# Revit family: Elite_Sliding_Window_XXXX_Standard
name_source: partatom
category: Windows
revit_build: Autodesk Revit 2014 (Build: 20130308_1515(x64)
units: mm (PartAtom-declared; Revit-internal decimal feet)

## types (41) — shared parameters
Astragal Sash Gap = 1 mm  [stored 0.00328084 ft]
Centered In Wall = Yes
Custom Sash Width Side = 800 mm  [stored 2.62467 ft]
Default Sill Height = 800 mm  [stored 2.62467 ft]
Description = Sliding window, XXXX
Equal Sash Width = Yes
Frame Thickness = 70 mm
Limit Sash Height Max = 1800 mm  [stored 5.90551 ft]
Limit Sash Height Min = 300 mm  [stored 0.984252 ft]
Limit Sash Width Max = 1500 mm  [stored 4.92126 ft]
Limit Sash Width Min = 300 mm  [stored 0.984252 ft]
Limit Sash Width Side Min = 300 mm  [stored 0.984252 ft]
Limit Window Height Min = 383 mm  [stored 1.25656 ft]
Limit Window Width Min = 1167 mm
Manufacturer = Crealco
Model = Elite
Sash Frame Seal = 1 mm  [stored 0.00328084 ft]
Sash Rail Fore Aft Spacing = 5 mm  [stored 0.0164042 ft]
Sash Side Spacing = 1 mm  [stored 0.00328084 ft]
Wall Closure = By host
zero-valued in all types: Custom Frame Offset From Exterior

## per-type parameters (varying)
- Elite-2406XXXX-1000Pa: Area Middle Sash Glazing=0.23 m²; Area Side Sash Glazing=0.23 m²; Clearvue SHGC Value=0.496; Clearvue U Value=6.99; Custom Windload=1000 mm  [stored 3.28084 ft]; Custom Window Height=590 mm  [stored 1.9357 ft]; Custom Window Width=2390 mm  [stored 7.84121 ft]; Energy Advantage SHGC Value=0.447; Energy Advantage U Value=5.88; Height=590 mm  [stored 1.9357 ft]; Inside Heavy Duty Interlocker=No; Interlocker Configuration=0 mm  [stored 0 ft]; Intruderprufe LowE SHGC Value=0.418; Intruderprufe LowE U Value=5.71; Intruderprufe SHGC Value=0.472; Intruderprufe U Value=6.87; Limit Sash Width Side Max=912 mm; Limit Window Height Max=1883 mm; Limit Window Width Max=2990 mm  [stored 9.80971 ft]; Max Pane Area=0.23 m²; Outside Heavy Duty Interlocker=No; Sash Height=507 mm; Sash Width Middle=606 mm; Sash Width Sides=606 mm; URL=http://www.crealco.co.za; Width=2390 mm  [stored 7.84121 ft]; Windload Design=1000 mm  [stored 3.28084 ft]
- Elite-2706XXXX-1000Pa: Area Middle Sash Glazing=0.26 m²; Area Side Sash Glazing=0.26 m²; Clearvue SHGC Value=5.07; Clearvue U Value=6.96; Custom Windload=1000 mm  [stored 3.28084 ft]; Custom Window Height=590 mm  [stored 1.9357 ft]; Custom Window Width=2690 mm; Energy Advantage SHGC Value=0.456; Energy Advantage U Value=5.8; Height=590 mm  [stored 1.9357 ft]; Inside Heavy Duty Interlocker=No; Interlocker Configuration=0 mm  [stored 0 ft]; Intruderprufe LowE SHGC Value=0.426; Intruderprufe LowE U Value=5.64; Intruderprufe SHGC Value=0.482; Intruderprufe U Value=6.83; Limit Sash Width Side Max=1062 mm; Limit Window Height Max=1883 mm; Limit Window Width Max=2990 mm  [stored 9.80971 ft]; Max Pane Area=0.26 m²; Outside Heavy Duty Interlocker=No; Sash Height=507 mm; Sash Width Middle=681 mm; Sash Width Sides=681 mm; URL=http://www.crealco.co.za; Width=2690 mm; Windload Design=1000 mm  [stored 3.28084 ft]
- Elite-3006XXXX-1000Pa: Area Middle Sash Glazing=0.29 m²; Area Side Sash Glazing=0.29 m²; Clearvue SHGC Value=0.515; Clearvue U Value=6.93; Custom Windload=1000 mm  [stored 3.28084 ft]; Custom Window Height=590 mm  [stored 1.9357 ft]; Custom Window Width=2990 mm  [stored 9.80971 ft]; Energy Advantage SHGC Value=0.464; Energy Advantage U Value=5.74; Height=590 mm  [stored 1.9357 ft]; Inside Heavy Duty Interlocker=No; Interlocker Configuration=0 mm  [stored 0 ft]; Intruderprufe LowE SHGC Value=0.433; Intruderprufe LowE U Value=5.59; Intruderprufe SHGC Value=0.49; Intruderprufe U Value=6.8; Limit Sash Width Side Max=1212 mm; Limit Window Height Max=1883 mm; Limit Window Width Max=2990 mm  [stored 9.80971 ft]; Max Pane Area=0.29 m²; Outside Heavy Duty Interlocker=No; Sash Height=507 mm; Sash Width Middle=756 mm; Sash Width Sides=756 mm; URL=http://www.crealco.co.za; Width=2990 mm  [stored 9.80971 ft]; Windload Design=1000 mm  [stored 3.28084 ft]
- Elite-2409XXXX-1000Pa: Area Middle Sash Glazing=0.39 m²; Area Side Sash Glazing=0.39 m²; Clearvue SHGC Value=0.568; Clearvue U Value=6.82; Custom Windload=1000 mm  [stored 3.28084 ft]; Custom Window Height=890 mm  [stored 2.91995 ft]; Custom Window Width=2390 mm  [stored 7.84121 ft]; Energy Advantage SHGC Value=0.51; Energy Advantage U Value=5.5; Height=890 mm  [stored 2.91995 ft]; Inside Heavy Duty Interlocker=No; Interlocker Configuration=0 mm  [stored 0 ft]; Intruderprufe LowE SHGC Value=0.476; Intruderprufe LowE U Value=5.33; Intruderprufe SHGC Value=0.539; Intruderprufe U Value=6.69; Limit Sash Width Side Max=912 mm; Limit Window Height Max=1883 mm; Limit Window Width Max=2990 mm  [stored 9.80971 ft]; Max Pane Area=0.39 m²; Outside Heavy Duty Interlocker=No; Sash Height=807 mm  [stored 2.64764 ft]; Sash Width Middle=606 mm; Sash Width Sides=606 mm; URL=http://www.crealco.co.za; Width=2390 mm  [stored 7.84121 ft]; Windload Design=1000 mm  [stored 3.28084 ft]
- Elite-2709XXXX-1000Pa: Area Middle Sash Glazing=0.44 m²; Area Side Sash Glazing=0.44 m²; Clearvue SHGC Value=0.58; Clearvue U Value=6.77; Custom Windload=1000 mm  [stored 3.28084 ft]; Custom Window Height=890 mm  [stored 2.91995 ft]; Custom Window Width=2690 mm; Energy Advantage SHGC Value=0.521; Energy Advantage U Value=5.41; Height=890 mm  [stored 2.91995 ft]; Inside Heavy Duty Interlocker=No; Interlocker Configuration=0 mm  [stored 0 ft]; Intruderprufe LowE SHGC Value=0.486; Intruderprufe LowE U Value=5.25; Intruderprufe SHGC Value=0.551; Intruderprufe U Value=6.64; Limit Sash Width Side Max=1062 mm; Limit Window Height Max=1883 mm; Limit Window Width Max=2990 mm  [stored 9.80971 ft]; Max Pane Area=0.44 m²; Outside Heavy Duty Interlocker=No; Sash Height=807 mm  [stored 2.64764 ft]; Sash Width Middle=681 mm; Sash Width Sides=681 mm; URL=http://www.crealco.co.za; Width=2690 mm; Windload Design=1000 mm  [stored 3.28084 ft]
- Elite-3009XXXX-1000Pa: Area Middle Sash Glazing=0.5 m²; Area Side Sash Glazing=0.5 m²; Clearvue SHGC Value=0.515; Clearvue U Value=6.93; Custom Windload=1000 mm  [stored 3.28084 ft]; Custom Window Height=890 mm  [stored 2.91995 ft]; Custom Window Width=2990 mm  [stored 9.80971 ft]; Energy Advantage SHGC Value=0.464; Energy Advantage U Value=5.74; Height=890 mm  [stored 2.91995 ft]; Inside Heavy Duty Interlocker=No; Interlocker Configuration=0 mm  [stored 0 ft]; Intruderprufe LowE SHGC Value=0.433; Intruderprufe LowE U Value=5.59; Intruderprufe SHGC Value=0.49; Intruderprufe U Value=6.8; Limit Sash Width Side Max=1212 mm; Limit Window Height Max=1883 mm; Limit Window Width Max=2990 mm  [stored 9.80971 ft]; Max Pane Area=0.5 m²; Outside Heavy Duty Interlocker=No; Sash Height=807 mm  [stored 2.64764 ft]; Sash Width Middle=756 mm; Sash Width Sides=756 mm; URL=http://www.crealco.co.za; Width=2990 mm  [stored 9.80971 ft]; Windload Design=1000 mm  [stored 3.28084 ft]
- Elite-2412XXXX-1000Pa: Area Middle Sash Glazing=0.55 m²; Area Side Sash Glazing=0.55 m²; Clearvue SHGC Value=0.603; Clearvue U Value=6.73; Custom Windload=1000 mm  [stored 3.28084 ft]; Custom Window Height=1190 mm  [stored 3.9042 ft]; Custom Window Width=2390 mm  [stored 7.84121 ft]; Energy Advantage SHGC Value=0.542; Energy Advantage U Value=5.32; Height=1190 mm  [stored 3.9042 ft]; Inside Heavy Duty Interlocker=No; Interlocker Configuration=0 mm  [stored 0 ft]; Intruderprufe LowE SHGC Value=0.505; Intruderprufe LowE U Value=5.15; Intruderprufe SHGC Value=0.572; Intruderprufe U Value=6.6; Limit Sash Width Side Max=912 mm; Limit Window Height Max=1883 mm; Limit Window Width Max=2990 mm  [stored 9.80971 ft]; Max Pane Area=0.55 m²; Outside Heavy Duty Interlocker=No; Sash Height=1107 mm  [stored 3.63189 ft]; Sash Width Middle=606 mm; Sash Width Sides=606 mm; URL=www.crealco.co.za; Width=2390 mm  [stored 7.84121 ft]; Windload Design=1000 mm  [stored 3.28084 ft]
- Elite-2712XXXX-1000Pa: Area Middle Sash Glazing=0.63 m²; Area Side Sash Glazing=0.63 m²; Clearvue SHGC Value=0.616; Clearvue U Value=6.68; Custom Windload=1000 mm  [stored 3.28084 ft]; Custom Window Height=1190 mm  [stored 3.9042 ft]; Custom Window Width=2690 mm; Energy Advantage SHGC Value=0.553; Energy Advantage U Value=5.22; Height=1190 mm  [stored 3.9042 ft]; Inside Heavy Duty Interlocker=No; Interlocker Configuration=0 mm  [stored 0 ft]; Intruderprufe LowE SHGC Value=0.515; Intruderprufe LowE U Value=5.306; Intruderprufe SHGC Value=0.585; Intruderprufe U Value=6.55; Limit Sash Width Side Max=1062 mm; Limit Window Height Max=1883 mm; Limit Window Width Max=2990 mm  [stored 9.80971 ft]; Max Pane Area=0.63 m²; Outside Heavy Duty Interlocker=No; Sash Height=1107 mm  [stored 3.63189 ft]; Sash Width Middle=681 mm; Sash Width Sides=681 mm; URL=http://www.crealco.co.za; Width=2690 mm; Windload Design=1000 mm  [stored 3.28084 ft]
- Elite-3012XXXX-1000Pa: Area Middle Sash Glazing=0.7 m²; Area Side Sash Glazing=0.7 m²; Clearvue SHGC Value=0.627; Clearvue U Value=6.64; Custom Windload=1000 mm  [stored 3.28084 ft]; Custom Window Height=1190 mm  [stored 3.9042 ft]; Custom Window Width=2990 mm  [stored 9.80971 ft]; Energy Advantage SHGC Value=0.562; Energy Advantage U Value=5.144; Height=1190 mm  [stored 3.9042 ft]; Inside Heavy Duty Interlocker=No; Interlocker Configuration=0 mm  [stored 0 ft]; Intruderprufe LowE SHGC Value=0.524; Intruderprufe LowE U Value=4.99; Intruderprufe SHGC Value=0.595; Intruderprufe U Value=6.51; Limit Sash Width Side Max=1212 mm; Limit Window Height Max=1883 mm; Limit Window Width Max=2990 mm  [stored 9.80971 ft]; Max Pane Area=0.7 m²; Outside Heavy Duty Interlocker=No; Sash Height=1107 mm  [stored 3.63189 ft]; Sash Width Middle=756 mm; Sash Width Sides=756 mm; URL=http://www.crealco.co.za; Width=2990 mm  [stored 9.80971 ft]; Windload Design=1000 mm  [stored 3.28084 ft]
- Elite-2415XXXX-1000Pa: Area Middle Sash Glazing=0.72 m²; Area Side Sash Glazing=0.72 m²; Clearvue SHGC Value=0.624; Clearvue U Value=6.68; Custom Windload=1000 mm  [stored 3.28084 ft]; Custom Window Height=1490 mm  [stored 4.88845 ft]; Custom Window Width=2390 mm  [stored 7.84121 ft]; Energy Advantage SHGC Value=0.56; Energy Advantage U Value=5.21; Height=1490 mm  [stored 4.88845 ft]; Inside Heavy Duty Interlocker=Yes; Interlocker Configuration=1 mm  [stored 0.00328084 ft]; Intruderprufe LowE SHGC Value=0.522; Intruderprufe LowE U Value=5.04; Intruderprufe SHGC Value=0.592; Intruderprufe U Value=6.55; Limit Sash Width Side Max=912 mm; Limit Window Height Max=1883 mm; Limit Window Width Max=2990 mm  [stored 9.80971 ft]; Max Pane Area=0.72 m²; Outside Heavy Duty Interlocker=No; Sash Height=1407 mm  [stored 4.61614 ft]; Sash Width Middle=606 mm; Sash Width Sides=606 mm; URL=http://www.crealco.co.za; Width=2390 mm  [stored 7.84121 ft]; Windload Design=1000 mm  [stored 3.28084 ft]
- Elite-2715XXXX-1000Pa: Area Middle Sash Glazing=0.81 m²; Area Side Sash Glazing=0.81 m²; Clearvue SHGC Value=0.638; Clearvue U Value=6.692; Custom Windload=1000 mm  [stored 3.28084 ft]; Custom Window Height=1490 mm  [stored 4.88845 ft]; Custom Window Width=2690 mm; Energy Advantage SHGC Value=0.572; Energy Advantage U Value=5.11; Height=1490 mm  [stored 4.88845 ft]; Inside Heavy Duty Interlocker=Yes; Interlocker Configuration=1 mm  [stored 0.00328084 ft]; Intruderprufe LowE SHGC Value=0.533; Intruderprufe LowE U Value=4.95; Intruderprufe SHGC Value=0.605; Intruderprufe U Value=6.49; Limit Sash Width Side Max=1062 mm; Limit Window Height Max=1883 mm; Limit Window Width Max=2990 mm  [stored 9.80971 ft]; Max Pane Area=0.81 m²; Outside Heavy Duty Interlocker=No; Sash Height=1407 mm  [stored 4.61614 ft]; Sash Width Middle=681 mm; Sash Width Sides=681 mm; URL=http://www.crealco.co.za; Width=2690 mm; Windload Design=1000 mm  [stored 3.28084 ft]
- Elite-3015XXXX-1000Pa: Area Middle Sash Glazing=0.91 m²; Area Side Sash Glazing=0.91 m²; Clearvue SHGC Value=0.649; Clearvue U Value=6.58; Custom Windload=1000 mm  [stored 3.28084 ft]; Custom Window Height=1490 mm  [stored 4.88845 ft]; Custom Window Width=2990 mm  [stored 9.80971 ft]; Energy Advantage SHGC Value=0.582; Energy Advantage U Value=5.02; Height=1490 mm  [stored 4.88845 ft]; Inside Heavy Duty Interlocker=Yes; Interlocker Configuration=1 mm  [stored 0.00328084 ft]; Intruderprufe LowE SHGC Value=0.542; Intruderprufe LowE U Value=4.87; Intruderprufe SHGC Value=0.616; Intruderprufe U Value=6.45; Limit Sash Width Side Max=1212 mm; Limit Window Height Max=1883 mm; Limit Window Width Max=2990 mm  [stored 9.80971 ft]; Max Pane Area=0.91 m²; Outside Heavy Duty Interlocker=No; Sash Height=1407 mm  [stored 4.61614 ft]; Sash Width Middle=756 mm; Sash Width Sides=756 mm; URL=http://www.crealco.co.za; Width=2990 mm  [stored 9.80971 ft]; Windload Design=1000 mm  [stored 3.28084 ft]
- Elite-2418XXXX-1000Pa: Area Middle Sash Glazing=0.88 m²; Area Side Sash Glazing=0.88 m²; Clearvue SHGC Value=0.638; Clearvue U Value=6.65; Custom Windload=1000 mm  [stored 3.28084 ft]; Custom Window Height=1790 mm  [stored 5.8727 ft]; Custom Window Width=2390 mm  [stored 7.84121 ft]; Energy Advantage SHGC Value=0.573; Energy Advantage U Value=5.13; Height=1790 mm  [stored 5.8727 ft]; Inside Heavy Duty Interlocker=Yes; Interlocker Configuration=1 mm  [stored 0.00328084 ft]; Intruderprufe LowE SHGC Value=0.533; Intruderprufe LowE U Value=4.97; Intruderprufe SHGC Value=0.606; Intruderprufe U Value=6.51; Limit Sash Width Side Max=912 mm; Limit Window Height Max=1883 mm; Limit Window Width Max=2990 mm  [stored 9.80971 ft]; Max Pane Area=0.88 m²; Outside Heavy Duty Interlocker=No; Sash Height=1707 mm; Sash Width Middle=606 mm; Sash Width Sides=606 mm; URL=http://www.crealco.co.za; Width=2390 mm  [stored 7.84121 ft]; Windload Design=1000 mm  [stored 3.28084 ft]
- Elite-2718XXXX-1000Pa: Area Middle Sash Glazing=1 m²; Area Side Sash Glazing=1 m²; Clearvue SHGC Value=0.652; Clearvue U Value=6.59; Custom Windload=1000 mm  [stored 3.28084 ft]; Custom Window Height=1790 mm  [stored 5.8727 ft]; Custom Window Width=2690 mm; Energy Advantage SHGC Value=0.585; Energy Advantage U Value=5.03; Height=1790 mm  [stored 5.8727 ft]; Inside Heavy Duty Interlocker=Yes; Interlocker Configuration=2 mm  [stored 0.00656168 ft]; Intruderprufe LowE SHGC Value=0.545; Intruderprufe LowE U Value=4.87; Intruderprufe SHGC Value=0.619; Intruderprufe U Value=6.46; Limit Sash Width Side Max=1062 mm; Limit Window Height Max=1883 mm; Limit Window Width Max=2990 mm  [stored 9.80971 ft]; Max Pane Area=1 m²; Outside Heavy Duty Interlocker=Yes; Sash Height=1707 mm; Sash Width Middle=681 mm; Sash Width Sides=681 mm; URL=http://www.crealco.co.za; Width=2690 mm; Windload Design=1000 mm  [stored 3.28084 ft]
- Elite-3018XXXX-1000Pa: Area Middle Sash Glazing=1.12 m²; Area Side Sash Glazing=1.12 m²; Clearvue SHGC Value=0.664; Clearvue U Value=6.54; Custom Windload=1000 mm  [stored 3.28084 ft]; Custom Window Height=1790 mm  [stored 5.8727 ft]; Custom Window Width=2990 mm  [stored 9.80971 ft]; Energy Advantage SHGC Value=0.595; Energy Advantage U Value=4.95; Height=1790 mm  [stored 5.8727 ft]; Inside Heavy Duty Interlocker=Yes; Interlocker Configuration=2 mm  [stored 0.00656168 ft]; Intruderprufe LowE SHGC Value=0.554; Intruderprufe LowE U Value=4.8; Intruderprufe SHGC Value=0.063; Intruderprufe U Value=6.41; Limit Sash Width Side Max=1212 mm; Limit Window Height Max=1883 mm; Limit Window Width Max=2990 mm  [stored 9.80971 ft]; Max Pane Area=1.12 m²; Outside Heavy Duty Interlocker=Yes; Sash Height=1707 mm; Sash Width Middle=756 mm; Sash Width Sides=756 mm; URL=http://www.crealco.co.za; Width=2990 mm  [stored 9.80971 ft]; Windload Design=1000 mm  [stored 3.28084 ft]
- Elite-2406XXXX-1500Pa: Area Middle Sash Glazing=0.23 m²; Area Side Sash Glazing=0.23 m²; Clearvue SHGC Value=0.496; Clearvue U Value=6.99; Custom Windload=1500 mm  [stored 4.92126 ft]; Custom Window Height=590 mm  [stored 1.9357 ft]; Custom Window Width=2390 mm  [stored 7.84121 ft]; Energy Advantage SHGC Value=0.447; Energy Advantage U Value=5.88; Height=590 mm  [stored 1.9357 ft]; Inside Heavy Duty Interlocker=No; Interlocker Configuration=0 mm  [stored 0 ft]; Intruderprufe LowE SHGC Value=0.418; Intruderprufe LowE U Value=5.71; Intruderprufe SHGC Value=0.472; Intruderprufe U Value=6.87; Limit Sash Width Side Max=912 mm; Limit Window Height Max=1883 mm; Limit Window Width Max=2990 mm  [stored 9.80971 ft]; Max Pane Area=0.23 m²; Outside Heavy Duty Interlocker=No; Sash Height=507 mm; Sash Width Middle=606 mm; Sash Width Sides=606 mm; URL=http://www.crealco.co.za; Width=2390 mm  [stored 7.84121 ft]; Windload Design=1500 mm  [stored 4.92126 ft]
- Elite-2406XXXX-2000Pa: Area Middle Sash Glazing=0.23 m²; Area Side Sash Glazing=0.23 m²; Clearvue SHGC Value=0.496; Clearvue U Value=6.99; Custom Windload=2000 mm  [stored 6.56168 ft]; Custom Window Height=590 mm  [stored 1.9357 ft]; Custom Window Width=2390 mm  [stored 7.84121 ft]; Energy Advantage SHGC Value=0.447; Energy Advantage U Value=5.88; Height=590 mm  [stored 1.9357 ft]; Inside Heavy Duty Interlocker=No; Interlocker Configuration=0 mm  [stored 0 ft]; Intruderprufe LowE SHGC Value=0.418; Intruderprufe LowE U Value=5.71; Intruderprufe SHGC Value=0.472; Intruderprufe U Value=6.87; Limit Sash Width Side Max=912 mm; Limit Window Height Max=1490 mm  [stored 4.88845 ft]; Limit Window Width Max=2990 mm  [stored 9.80971 ft]; Max Pane Area=0.23 m²; Outside Heavy Duty Interlocker=No; Sash Height=507 mm; Sash Width Middle=606 mm; Sash Width Sides=606 mm; URL=http://www.crealco.co.za; Width=2390 mm  [stored 7.84121 ft]; Windload Design=2000 mm  [stored 6.56168 ft]
- Elite-2409XXXX-1500Pa: Area Middle Sash Glazing=0.39 m²; Area Side Sash Glazing=0.39 m²; Clearvue SHGC Value=0.568; Clearvue U Value=6.82; Custom Windload=1500 mm  [stored 4.92126 ft]; Custom Window Height=890 mm  [stored 2.91995 ft]; Custom Window Width=2390 mm  [stored 7.84121 ft]; Energy Advantage SHGC Value=0.51; Energy Advantage U Value=5.5; Height=890 mm  [stored 2.91995 ft]; Inside Heavy Duty Interlocker=No; Interlocker Configuration=0 mm  [stored 0 ft]; Intruderprufe LowE SHGC Value=0.476; Intruderprufe LowE U Value=5.33; Intruderprufe SHGC Value=0.539; Intruderprufe U Value=6.69; Limit Sash Width Side Max=912 mm; Limit Window Height Max=1883 mm; Limit Window Width Max=2990 mm  [stored 9.80971 ft]; Max Pane Area=0.39 m²; Outside Heavy Duty Interlocker=No; Sash Height=807 mm  [stored 2.64764 ft]; Sash Width Middle=606 mm; Sash Width Sides=606 mm; URL=http://www.crealco.co.za; Width=2390 mm  [stored 7.84121 ft]; Windload Design=1500 mm  [stored 4.92126 ft]
- Elite-2409XXXX-2000Pa: Area Middle Sash Glazing=0.39 m²; Area Side Sash Glazing=0.39 m²; Clearvue SHGC Value=0.568; Clearvue U Value=6.82; Custom Windload=2000 mm  [stored 6.56168 ft]; Custom Window Height=890 mm  [stored 2.91995 ft]; Custom Window Width=2390 mm  [stored 7.84121 ft]; Energy Advantage SHGC Value=0.51; Energy Advantage U Value=5.5; Height=890 mm  [stored 2.91995 ft]; Inside Heavy Duty Interlocker=No; Interlocker Configuration=0 mm  [stored 0 ft]; Intruderprufe LowE SHGC Value=0.476; Intruderprufe LowE U Value=5.33; Intruderprufe SHGC Value=0.539; Intruderprufe U Value=6.69; Limit Sash Width Side Max=912 mm; Limit Window Height Max=1490 mm  [stored 4.88845 ft]; Limit Window Width Max=2990 mm  [stored 9.80971 ft]; Max Pane Area=0.39 m²; Outside Heavy Duty Interlocker=No; Sash Height=807 mm  [stored 2.64764 ft]; Sash Width Middle=606 mm; Sash Width Sides=606 mm; URL=http://www.crealco.co.za; Width=2390 mm  [stored 7.84121 ft]; Windload Design=2000 mm  [stored 6.56168 ft]
- Elite-2412XXXX-1500Pa: Area Middle Sash Glazing=0.55 m²; Area Side Sash Glazing=0.55 m²; Clearvue SHGC Value=0.603; Clearvue U Value=6.73; Custom Windload=1500 mm  [stored 4.92126 ft]; Custom Window Height=1190 mm  [stored 3.9042 ft]; Custom Window Width=2390 mm  [stored 7.84121 ft]; Energy Advantage SHGC Value=0.542; Energy Advantage U Value=5.32; Height=1190 mm  [stored 3.9042 ft]; Inside Heavy Duty Interlocker=No; Interlocker Configuration=0 mm  [stored 0 ft]; Intruderprufe LowE SHGC Value=0.505; Intruderprufe LowE U Value=5.15; Intruderprufe SHGC Value=0.572; Intruderprufe U Value=6.6; Limit Sash Width Side Max=912 mm; Limit Window Height Max=1883 mm; Limit Window Width Max=2990 mm  [stored 9.80971 ft]; Max Pane Area=0.55 m²; Outside Heavy Duty Interlocker=No; Sash Height=1107 mm  [stored 3.63189 ft]; Sash Width Middle=606 mm; Sash Width Sides=606 mm; URL=http://www.crealco.co.za; Width=2390 mm  [stored 7.84121 ft]; Windload Design=1500 mm  [stored 4.92126 ft]
- Elite-2412XXXX-2000Pa: Area Middle Sash Glazing=0.55 m²; Area Side Sash Glazing=0.55 m²; Clearvue SHGC Value=0.603; Clearvue U Value=6.73; Custom Windload=2000 mm  [stored 6.56168 ft]; Custom Window Height=1190 mm  [stored 3.9042 ft]; Custom Window Width=2390 mm  [stored 7.84121 ft]; Energy Advantage SHGC Value=0.542; Energy Advantage U Value=5.32; Height=1190 mm  [stored 3.9042 ft]; Inside Heavy Duty Interlocker=Yes; Interlocker Configuration=1 mm  [stored 0.00328084 ft]; Intruderprufe LowE SHGC Value=0.505; Intruderprufe LowE U Value=5.15; Intruderprufe SHGC Value=0.572; Intruderprufe U Value=6.6; Limit Sash Width Side Max=912 mm; Limit Window Height Max=1490 mm  [stored 4.88845 ft]; Limit Window Width Max=2990 mm  [stored 9.80971 ft]; Max Pane Area=0.55 m²; Outside Heavy Duty Interlocker=No; Sash Height=1107 mm  [stored 3.63189 ft]; Sash Width Middle=606 mm; Sash Width Sides=606 mm; URL=http://www.crealco.co.za; Width=2390 mm  [stored 7.84121 ft]; Windload Design=2000 mm  [stored 6.56168 ft]
- Elite-2415XXXX-1500Pa: Area Middle Sash Glazing=0.72 m²; Area Side Sash Glazing=0.72 m²; Clearvue SHGC Value=0.624; Clearvue U Value=6.68; Custom Windload=1500 mm  [stored 4.92126 ft]; Custom Window Height=1490 mm  [stored 4.88845 ft]; Custom Window Width=2390 mm  [stored 7.84121 ft]; Energy Advantage SHGC Value=0.56; Energy Advantage U Value=5.21; Height=1490 mm  [stored 4.88845 ft]; Inside Heavy Duty Interlocker=Yes; Interlocker Configuration=1 mm  [stored 0.00328084 ft]; Intruderprufe LowE SHGC Value=0.522; Intruderprufe LowE U Value=5.04; Intruderprufe SHGC Value=0.592; Intruderprufe U Value=6.55; Limit Sash Width Side Max=912 mm; Limit Window Height Max=1883 mm; Limit Window Width Max=2990 mm  [stored 9.80971 ft]; Max Pane Area=0.72 m²; Outside Heavy Duty Interlocker=No; Sash Height=1407 mm  [stored 4.61614 ft]; Sash Width Middle=606 mm; Sash Width Sides=606 mm; URL=http://www.crealco.co.za; Width=2390 mm  [stored 7.84121 ft]; Windload Design=1500 mm  [stored 4.92126 ft]
- Elite-2415XXXX-2000Pa: Area Middle Sash Glazing=0.72 m²; Area Side Sash Glazing=0.72 m²; Clearvue SHGC Value=0.624; Clearvue U Value=6.68; Custom Windload=2000 mm  [stored 6.56168 ft]; Custom Window Height=1490 mm  [stored 4.88845 ft]; Custom Window Width=2390 mm  [stored 7.84121 ft]; Energy Advantage SHGC Value=0.56; Energy Advantage U Value=5.21; Height=1490 mm  [stored 4.88845 ft]; Inside Heavy Duty Interlocker=Yes; Interlocker Configuration=1 mm  [stored 0.00328084 ft]; Intruderprufe LowE SHGC Value=0.522; Intruderprufe LowE U Value=5.04; Intruderprufe SHGC Value=0.592; Intruderprufe U Value=6.55; Limit Sash Width Side Max=912 mm; Limit Window Height Max=1490 mm  [stored 4.88845 ft]; Limit Window Width Max=2990 mm  [stored 9.80971 ft]; Max Pane Area=0.72 m²; Outside Heavy Duty Interlocker=No; Sash Height=1407 mm  [stored 4.61614 ft]; Sash Width Middle=606 mm; Sash Width Sides=606 mm; URL=http://www.crealco.co.za; Width=2390 mm  [stored 7.84121 ft]; Windload Design=2000 mm  [stored 6.56168 ft]
- Elite-2418XXXX-1500Pa: Area Middle Sash Glazing=0.88 m²; Area Side Sash Glazing=0.88 m²; Clearvue SHGC Value=0.638; Clearvue U Value=6.65; Custom Windload=1500 mm  [stored 4.92126 ft]; Custom Window Height=1790 mm  [stored 5.8727 ft]; Custom Window Width=2390 mm  [stored 7.84121 ft]; Energy Advantage SHGC Value=0.573; Energy Advantage U Value=5.13; Height=1790 mm  [stored 5.8727 ft]; Inside Heavy Duty Interlocker=Yes; Interlocker Configuration=2 mm  [stored 0.00656168 ft]; Intruderprufe LowE SHGC Value=0.533; Intruderprufe LowE U Value=4.97; Intruderprufe SHGC Value=0.606; Intruderprufe U Value=6.51; Limit Sash Width Side Max=912 mm; Limit Window Height Max=1883 mm; Limit Window Width Max=2690 mm; Max Pane Area=0.88 m²; Outside Heavy Duty Interlocker=Yes; Sash Height=1707 mm; Sash Width Middle=606 mm; Sash Width Sides=606 mm; URL=http://www.crealco.co.za; Width=2390 mm  [stored 7.84121 ft]; Windload Design=1500 mm  [stored 4.92126 ft]
- Elite-2706XXXX-1500Pa: Area Middle Sash Glazing=0.26 m²; Area Side Sash Glazing=0.26 m²; Clearvue SHGC Value=5.07; Clearvue U Value=6.96; Custom Windload=1500 mm  [stored 4.92126 ft]; Custom Window Height=590 mm  [stored 1.9357 ft]; Custom Window Width=2690 mm; Energy Advantage SHGC Value=0.456; Energy Advantage U Value=5.8; Height=590 mm  [stored 1.9357 ft]; Inside Heavy Duty Interlocker=No; Interlocker Configuration=0 mm  [stored 0 ft]; Intruderprufe LowE SHGC Value=0.426; Intruderprufe LowE U Value=5.64; Intruderprufe SHGC Value=0.482; Intruderprufe U Value=6.83; Limit Sash Width Side Max=1062 mm; Limit Window Height Max=1883 mm; Limit Window Width Max=2990 mm  [stored 9.80971 ft]; Max Pane Area=0.26 m²; Outside Heavy Duty Interlocker=No; Sash Height=507 mm; Sash Width Middle=681 mm; Sash Width Sides=681 mm; URL=http://www.crealco.co.za; Width=2690 mm; Windload Design=1500 mm  [stored 4.92126 ft]
- Elite-2706XXXX-2000Pa: Area Middle Sash Glazing=0.26 m²; Area Side Sash Glazing=0.26 m²; Clearvue SHGC Value=5.07; Clearvue U Value=6.96; Custom Windload=2000 mm  [stored 6.56168 ft]; Custom Window Height=590 mm  [stored 1.9357 ft]; Custom Window Width=2690 mm; Energy Advantage SHGC Value=0.456; Energy Advantage U Value=5.8; Height=590 mm  [stored 1.9357 ft]; Inside Heavy Duty Interlocker=No; Interlocker Configuration=0 mm  [stored 0 ft]; Intruderprufe LowE SHGC Value=0.426; Intruderprufe LowE U Value=5.64; Intruderprufe SHGC Value=0.482; Intruderprufe U Value=6.83; Limit Sash Width Side Max=1062 mm; Limit Window Height Max=1490 mm  [stored 4.88845 ft]; Limit Window Width Max=2990 mm  [stored 9.80971 ft]; Max Pane Area=0.26 m²; Outside Heavy Duty Interlocker=No; Sash Height=507 mm; Sash Width Middle=681 mm; Sash Width Sides=681 mm; URL=http://www.crealco.co.za; Width=2690 mm; Windload Design=2000 mm  [stored 6.56168 ft]
- Elite-2709XXXX-1500Pa: Area Middle Sash Glazing=0.44 m²; Area Side Sash Glazing=0.44 m²; Clearvue SHGC Value=0.58; Clearvue U Value=6.77; Custom Windload=1500 mm  [stored 4.92126 ft]; Custom Window Height=890 mm  [stored 2.91995 ft]; Custom Window Width=2690 mm; Energy Advantage SHGC Value=0.521; Energy Advantage U Value=5.41; Height=890 mm  [stored 2.91995 ft]; Inside Heavy Duty Interlocker=No; Interlocker Configuration=0 mm  [stored 0 ft]; Intruderprufe LowE SHGC Value=0.486; Intruderprufe LowE U Value=5.25; Intruderprufe SHGC Value=0.551; Intruderprufe U Value=6.64; Limit Sash Width Side Max=1062 mm; Limit Window Height Max=1883 mm; Limit Window Width Max=2990 mm  [stored 9.80971 ft]; Max Pane Area=0.44 m²; Outside Heavy Duty Interlocker=No; Sash Height=807 mm  [stored 2.64764 ft]; Sash Width Middle=681 mm; Sash Width Sides=681 mm; URL=http://www.crealco.co.za; Width=2690 mm; Windload Design=1500 mm  [stored 4.92126 ft]
- Elite-2709XXXX-2000Pa: Area Middle Sash Glazing=0.44 m²; Area Side Sash Glazing=0.44 m²; Clearvue SHGC Value=0.58; Clearvue U Value=6.77; Custom Windload=2000 mm  [stored 6.56168 ft]; Custom Window Height=890 mm  [stored 2.91995 ft]; Custom Window Width=2690 mm; Energy Advantage SHGC Value=0.521; Energy Advantage U Value=5.41; Height=890 mm  [stored 2.91995 ft]; Inside Heavy Duty Interlocker=No; Interlocker Configuration=0 mm  [stored 0 ft]; Intruderprufe LowE SHGC Value=0.486; Intruderprufe LowE U Value=5.25; Intruderprufe SHGC Value=0.551; Intruderprufe U Value=6.64; Limit Sash Width Side Max=1062 mm; Limit Window Height Max=1490 mm  [stored 4.88845 ft]; Limit Window Width Max=2990 mm  [stored 9.80971 ft]; Max Pane Area=0.44 m²; Outside Heavy Duty Interlocker=No; Sash Height=807 mm  [stored 2.64764 ft]; Sash Width Middle=681 mm; Sash Width Sides=681 mm; URL=http://www.crealco.co.za; Width=2690 mm; Windload Design=2000 mm  [stored 6.56168 ft]
- Elite-2712XXXX-1500Pa: Area Middle Sash Glazing=0.63 m²; Area Side Sash Glazing=0.63 m²; Clearvue SHGC Value=0.616; Clearvue U Value=6.68; Custom Windload=1500 mm  [stored 4.92126 ft]; Custom Window Height=1190 mm  [stored 3.9042 ft]; Custom Window Width=2690 mm; Energy Advantage SHGC Value=0.553; Energy Advantage U Value=5.22; Height=1190 mm  [stored 3.9042 ft]; Inside Heavy Duty Interlocker=No; Interlocker Configuration=0 mm  [stored 0 ft]; Intruderprufe LowE SHGC Value=0.515; Intruderprufe LowE U Value=5.306; Intruderprufe SHGC Value=0.585; Intruderprufe U Value=6.55; Limit Sash Width Side Max=1062 mm; Limit Window Height Max=1883 mm; Limit Window Width Max=2990 mm  [stored 9.80971 ft]; Max Pane Area=0.63 m²; Outside Heavy Duty Interlocker=No; Sash Height=1107 mm  [stored 3.63189 ft]; Sash Width Middle=681 mm; Sash Width Sides=681 mm; URL=http://www.crealco.co.za; Width=2690 mm; Windload Design=1500 mm  [stored 4.92126 ft]
- Elite-2712XXXX-2000Pa: Area Middle Sash Glazing=0.63 m²; Area Side Sash Glazing=0.63 m²; Clearvue SHGC Value=0.616; Clearvue U Value=6.68; Custom Windload=2000 mm  [stored 6.56168 ft]; Custom Window Height=1190 mm  [stored 3.9042 ft]; Custom Window Width=2690 mm; Energy Advantage SHGC Value=0.553; Energy Advantage U Value=5.22; Height=1190 mm  [stored 3.9042 ft]; Inside Heavy Duty Interlocker=Yes; Interlocker Configuration=1 mm  [stored 0.00328084 ft]; Intruderprufe LowE SHGC Value=0.515; Intruderprufe LowE U Value=5.306; Intruderprufe SHGC Value=0.585; Intruderprufe U Value=6.55; Limit Sash Width Side Max=1062 mm; Limit Window Height Max=1490 mm  [stored 4.88845 ft]; Limit Window Width Max=2990 mm  [stored 9.80971 ft]; Max Pane Area=0.63 m²; Outside Heavy Duty Interlocker=No; Sash Height=1107 mm  [stored 3.63189 ft]; Sash Width Middle=681 mm; Sash Width Sides=681 mm; URL=http://www.crealco.co.za; Width=2690 mm; Windload Design=2000 mm  [stored 6.56168 ft]
- Elite-2715XXXX-1500Pa: Area Middle Sash Glazing=0.81 m²; Area Side Sash Glazing=0.81 m²; Clearvue SHGC Value=0.638; Clearvue U Value=6.692; Custom Windload=1500 mm  [stored 4.92126 ft]; Custom Window Height=1490 mm  [stored 4.88845 ft]; Custom Window Width=2690 mm; Energy Advantage SHGC Value=0.572; Energy Advantage U Value=5.11; Height=1490 mm  [stored 4.88845 ft]; Inside Heavy Duty Interlocker=Yes; Interlocker Configuration=1 mm  [stored 0.00328084 ft]; Intruderprufe LowE SHGC Value=0.533; Intruderprufe LowE U Value=4.95; Intruderprufe SHGC Value=0.605; Intruderprufe U Value=6.49; Limit Sash Width Side Max=1062 mm; Limit Window Height Max=1883 mm; Limit Window Width Max=2990 mm  [stored 9.80971 ft]; Max Pane Area=0.81 m²; Outside Heavy Duty Interlocker=No; Sash Height=1407 mm  [stored 4.61614 ft]; Sash Width Middle=681 mm; Sash Width Sides=681 mm; URL=http://www.crealco.co.za; Width=2690 mm; Windload Design=1500 mm  [stored 4.92126 ft]
- Elite-2715XXXX-2000Pa: Area Middle Sash Glazing=0.81 m²; Area Side Sash Glazing=0.81 m²; Clearvue SHGC Value=0.638; Clearvue U Value=6.692; Custom Windload=2000 mm  [stored 6.56168 ft]; Custom Window Height=1490 mm  [stored 4.88845 ft]; Custom Window Width=2690 mm; Energy Advantage SHGC Value=0.572; Energy Advantage U Value=5.11; Height=1490 mm  [stored 4.88845 ft]; Inside Heavy Duty Interlocker=Yes; Interlocker Configuration=2 mm  [stored 0.00656168 ft]; Intruderprufe LowE SHGC Value=0.533; Intruderprufe LowE U Value=4.95; Intruderprufe SHGC Value=0.605; Intruderprufe U Value=6.49; Limit Sash Width Side Max=1062 mm; Limit Window Height Max=1490 mm  [stored 4.88845 ft]; Limit Window Width Max=2990 mm  [stored 9.80971 ft]; Max Pane Area=0.81 m²; Outside Heavy Duty Interlocker=Yes; Sash Height=1407 mm  [stored 4.61614 ft]; Sash Width Middle=681 mm; Sash Width Sides=681 mm; URL=http://www.crealco.co.za; Width=2690 mm; Windload Design=2000 mm  [stored 6.56168 ft]
- Elite-2718XXXX-1500Pa: Area Middle Sash Glazing=1 m²; Area Side Sash Glazing=1 m²; Clearvue SHGC Value=0.652; Clearvue U Value=6.59; Custom Windload=1500 mm  [stored 4.92126 ft]; Custom Window Height=1790 mm  [stored 5.8727 ft]; Custom Window Width=2690 mm; Energy Advantage SHGC Value=0.585; Energy Advantage U Value=5.03; Height=1790 mm  [stored 5.8727 ft]; Inside Heavy Duty Interlocker=Yes; Interlocker Configuration=2 mm  [stored 0.00656168 ft]; Intruderprufe LowE SHGC Value=0.545; Intruderprufe LowE U Value=4.87; Intruderprufe SHGC Value=0.619; Intruderprufe U Value=6.46; Limit Sash Width Side Max=1062 mm; Limit Window Height Max=1883 mm; Limit Window Width Max=2690 mm; Max Pane Area=1 m²; Outside Heavy Duty Interlocker=Yes; Sash Height=1707 mm; Sash Width Middle=681 mm; Sash Width Sides=681 mm; URL=http://www.crealco.co.za; Width=2690 mm; Windload Design=1500 mm  [stored 4.92126 ft]
- Elite-3006XXXX-1500Pa: Area Middle Sash Glazing=0.29 m²; Area Side Sash Glazing=0.29 m²; Clearvue SHGC Value=0.515; Clearvue U Value=6.93; Custom Windload=1500 mm  [stored 4.92126 ft]; Custom Window Height=590 mm  [stored 1.9357 ft]; Custom Window Width=2990 mm  [stored 9.80971 ft]; Energy Advantage SHGC Value=0.464; Energy Advantage U Value=5.74; Height=590 mm  [stored 1.9357 ft]; Inside Heavy Duty Interlocker=No; Interlocker Configuration=0 mm  [stored 0 ft]; Intruderprufe LowE SHGC Value=0.433; Intruderprufe LowE U Value=5.59; Intruderprufe SHGC Value=0.49; Intruderprufe U Value=6.8; Limit Sash Width Side Max=1212 mm; Limit Window Height Max=1883 mm; Limit Window Width Max=2990 mm  [stored 9.80971 ft]; Max Pane Area=0.29 m²; Outside Heavy Duty Interlocker=No; Sash Height=507 mm; Sash Width Middle=756 mm; Sash Width Sides=756 mm; URL=http://www.crealco.co.za; Width=2990 mm  [stored 9.80971 ft]; Windload Design=1500 mm  [stored 4.92126 ft]
- Elite-3006XXXX-2000Pa: Area Middle Sash Glazing=0.29 m²; Area Side Sash Glazing=0.29 m²; Clearvue SHGC Value=0.515; Clearvue U Value=6.93; Custom Windload=2000 mm  [stored 6.56168 ft]; Custom Window Height=590 mm  [stored 1.9357 ft]; Custom Window Width=2990 mm  [stored 9.80971 ft]; Energy Advantage SHGC Value=0.464; Energy Advantage U Value=5.74; Height=590 mm  [stored 1.9357 ft]; Inside Heavy Duty Interlocker=No; Interlocker Configuration=0 mm  [stored 0 ft]; Intruderprufe LowE SHGC Value=0.433; Intruderprufe LowE U Value=5.59; Intruderprufe SHGC Value=0.49; Intruderprufe U Value=6.8; Limit Sash Width Side Max=1212 mm; Limit Window Height Max=1490 mm  [stored 4.88845 ft]; Limit Window Width Max=2990 mm  [stored 9.80971 ft]; Max Pane Area=0.29 m²; Outside Heavy Duty Interlocker=No; Sash Height=507 mm; Sash Width Middle=756 mm; Sash Width Sides=756 mm; URL=http://www.crealco.co.za; Width=2990 mm  [stored 9.80971 ft]; Windload Design=2000 mm  [stored 6.56168 ft]
- Elite-3009XXXX-1500Pa: Area Middle Sash Glazing=0.5 m²; Area Side Sash Glazing=0.5 m²; Clearvue SHGC Value=0.515; Clearvue U Value=6.93; Custom Windload=1500 mm  [stored 4.92126 ft]; Custom Window Height=890 mm  [stored 2.91995 ft]; Custom Window Width=2990 mm  [stored 9.80971 ft]; Energy Advantage SHGC Value=0.464; Energy Advantage U Value=5.74; Height=890 mm  [stored 2.91995 ft]; Inside Heavy Duty Interlocker=No; Interlocker Configuration=0 mm  [stored 0 ft]; Intruderprufe LowE SHGC Value=0.433; Intruderprufe LowE U Value=5.59; Intruderprufe SHGC Value=0.49; Intruderprufe U Value=6.8; Limit Sash Width Side Max=1212 mm; Limit Window Height Max=1883 mm; Limit Window Width Max=2990 mm  [stored 9.80971 ft]; Max Pane Area=0.5 m²; Outside Heavy Duty Interlocker=No; Sash Height=807 mm  [stored 2.64764 ft]; Sash Width Middle=756 mm; Sash Width Sides=756 mm; URL=http://www.crealco.co.za; Width=2990 mm  [stored 9.80971 ft]; Windload Design=1500 mm  [stored 4.92126 ft]
- Elite-3009XXXX-2000Pa: Area Middle Sash Glazing=0.5 m²; Area Side Sash Glazing=0.5 m²; Clearvue SHGC Value=0.515; Clearvue U Value=6.93; Custom Windload=2000 mm  [stored 6.56168 ft]; Custom Window Height=890 mm  [stored 2.91995 ft]; Custom Window Width=2990 mm  [stored 9.80971 ft]; Energy Advantage SHGC Value=0.464; Energy Advantage U Value=5.74; Height=890 mm  [stored 2.91995 ft]; Inside Heavy Duty Interlocker=No; Interlocker Configuration=0 mm  [stored 0 ft]; Intruderprufe LowE SHGC Value=0.433; Intruderprufe LowE U Value=5.59; Intruderprufe SHGC Value=0.49; Intruderprufe U Value=6.8; Limit Sash Width Side Max=1212 mm; Limit Window Height Max=1490 mm  [stored 4.88845 ft]; Limit Window Width Max=2990 mm  [stored 9.80971 ft]; Max Pane Area=0.5 m²; Outside Heavy Duty Interlocker=No; Sash Height=807 mm  [stored 2.64764 ft]; Sash Width Middle=756 mm; Sash Width Sides=756 mm; URL=http://www.crealco.co.za; Width=2990 mm  [stored 9.80971 ft]; Windload Design=2000 mm  [stored 6.56168 ft]
- Elite-3012XXXX-1500Pa: Area Middle Sash Glazing=0.7 m²; Area Side Sash Glazing=0.7 m²; Clearvue SHGC Value=0.627; Clearvue U Value=6.64; Custom Windload=1500 mm  [stored 4.92126 ft]; Custom Window Height=1190 mm  [stored 3.9042 ft]; Custom Window Width=2990 mm  [stored 9.80971 ft]; Energy Advantage SHGC Value=0.562; Energy Advantage U Value=5.144; Height=1190 mm  [stored 3.9042 ft]; Inside Heavy Duty Interlocker=Yes; Interlocker Configuration=1 mm  [stored 0.00328084 ft]; Intruderprufe LowE SHGC Value=0.524; Intruderprufe LowE U Value=4.99; Intruderprufe SHGC Value=0.595; Intruderprufe U Value=6.51; Limit Sash Width Side Max=1212 mm; Limit Window Height Max=1883 mm; Limit Window Width Max=2990 mm  [stored 9.80971 ft]; Max Pane Area=0.7 m²; Outside Heavy Duty Interlocker=No; Sash Height=1107 mm  [stored 3.63189 ft]; Sash Width Middle=756 mm; Sash Width Sides=756 mm; URL=http://www.crealco.co.za; Width=2990 mm  [stored 9.80971 ft]; Windload Design=1500 mm  [stored 4.92126 ft]
- Elite-3012XXXX-2000Pa: Area Middle Sash Glazing=0.7 m²; Area Side Sash Glazing=0.7 m²; Clearvue SHGC Value=0.627; Clearvue U Value=6.64; Custom Windload=2000 mm  [stored 6.56168 ft]; Custom Window Height=1190 mm  [stored 3.9042 ft]; Custom Window Width=2990 mm  [stored 9.80971 ft]; Energy Advantage SHGC Value=0.562; Energy Advantage U Value=5.144; Height=1190 mm  [stored 3.9042 ft]; Inside Heavy Duty Interlocker=Yes; Interlocker Configuration=1 mm  [stored 0.00328084 ft]; Intruderprufe LowE SHGC Value=0.524; Intruderprufe LowE U Value=4.99; Intruderprufe SHGC Value=0.595; Intruderprufe U Value=6.51; Limit Sash Width Side Max=1212 mm; Limit Window Height Max=1490 mm  [stored 4.88845 ft]; Limit Window Width Max=2990 mm  [stored 9.80971 ft]; Max Pane Area=0.7 m²; Outside Heavy Duty Interlocker=No; Sash Height=1107 mm  [stored 3.63189 ft]; Sash Width Middle=756 mm; Sash Width Sides=756 mm; URL=http://www.crealco.co.za; Width=2990 mm  [stored 9.80971 ft]; Windload Design=2000 mm  [stored 6.56168 ft]
- Elite-3015XXXX-1500Pa: Area Middle Sash Glazing=0.91 m²; Area Side Sash Glazing=0.91 m²; Clearvue SHGC Value=0.649; Clearvue U Value=6.58; Custom Windload=1500 mm  [stored 4.92126 ft]; Custom Window Height=1490 mm  [stored 4.88845 ft]; Custom Window Width=2990 mm  [stored 9.80971 ft]; Energy Advantage SHGC Value=0.582; Energy Advantage U Value=5.02; Height=1490 mm  [stored 4.88845 ft]; Inside Heavy Duty Interlocker=Yes; Interlocker Configuration=1 mm  [stored 0.00328084 ft]; Intruderprufe LowE SHGC Value=0.542; Intruderprufe LowE U Value=4.87; Intruderprufe SHGC Value=0.616; Intruderprufe U Value=6.45; Limit Sash Width Side Max=1212 mm; Limit Window Height Max=1883 mm; Limit Window Width Max=2990 mm  [stored 9.80971 ft]; Max Pane Area=0.91 m²; Outside Heavy Duty Interlocker=No; Sash Height=1407 mm  [stored 4.61614 ft]; Sash Width Middle=756 mm; Sash Width Sides=756 mm; URL=http://www.crealco.co.za; Width=2990 mm  [stored 9.80971 ft]; Windload Design=1500 mm  [stored 4.92126 ft]
- Elite-3015XXXX-2000Pa: Area Middle Sash Glazing=0.91 m²; Area Side Sash Glazing=0.91 m²; Clearvue SHGC Value=0.649; Clearvue U Value=6.58; Custom Windload=2000 mm  [stored 6.56168 ft]; Custom Window Height=1490 mm  [stored 4.88845 ft]; Custom Window Width=2990 mm  [stored 9.80971 ft]; Energy Advantage SHGC Value=0.582; Energy Advantage U Value=5.02; Height=1490 mm  [stored 4.88845 ft]; Inside Heavy Duty Interlocker=Yes; Interlocker Configuration=2 mm  [stored 0.00656168 ft]; Intruderprufe LowE SHGC Value=0.542; Intruderprufe LowE U Value=4.87; Intruderprufe SHGC Value=0.616; Intruderprufe U Value=6.45; Limit Sash Width Side Max=1212 mm; Limit Window Height Max=1490 mm  [stored 4.88845 ft]; Limit Window Width Max=2990 mm  [stored 9.80971 ft]; Max Pane Area=0.91 m²; Outside Heavy Duty Interlocker=Yes; Sash Height=1407 mm  [stored 4.61614 ft]; Sash Width Middle=756 mm; Sash Width Sides=756 mm; URL=http://www.crealco.co.za; Width=2990 mm  [stored 9.80971 ft]; Windload Design=2000 mm  [stored 6.56168 ft]

note: [stored X ft] marks values corroborated as IEEE doubles in the binary element streams (Revit-internal decimal feet)

## geometry (parser evidence)
native form markers: Sweep x47
no freeform markers — native parametric forms only
